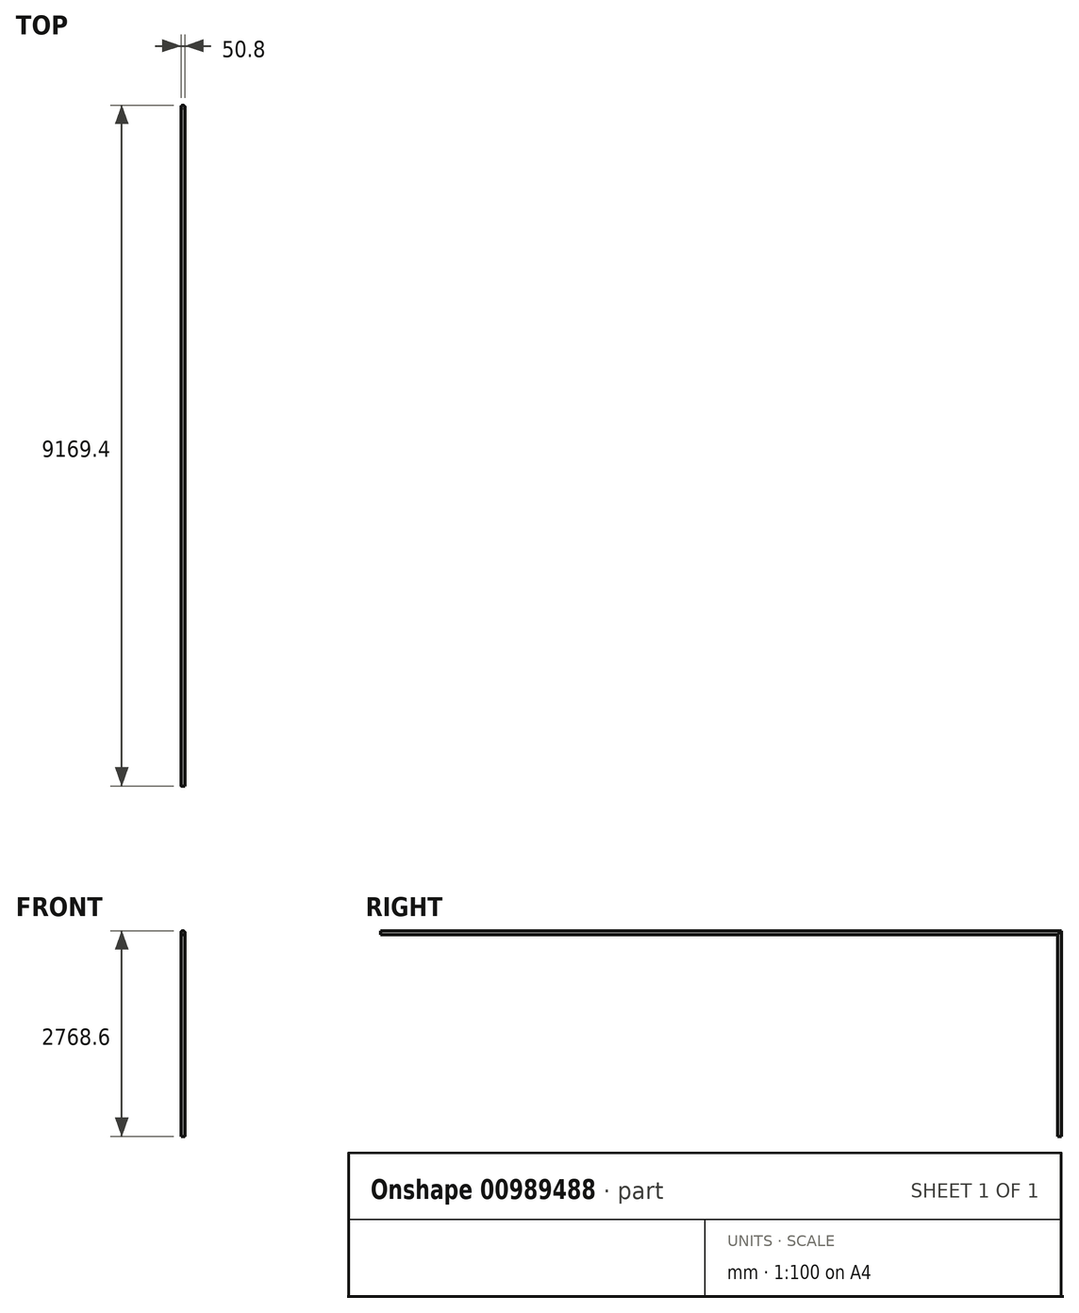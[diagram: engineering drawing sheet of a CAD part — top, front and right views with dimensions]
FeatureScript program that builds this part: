
annotation { "Feature Type Name" : "Feature", "Feature Type Description" : "" }
export const myFeature = defineFeature(function(context is Context, id is Id, definition is map)
    precondition{}
    {
        {
            var Q0;
            Q0=qCreatedBy(makeId("Front.planeOp"),FACE);
            var sketch = newSketch(context, id + "F0", { "sketchPlane" : qUnion([Q0])});
            skCircle(sketch, "E0", {"center": v(0, 0) * mm, "radius": 25.4 * mm});
            skSolve(sketch);
        }
        {
            var Q0;
            Q0=qCreatedBy(makeId("Right.planeOp"),FACE);
            var sketch = newSketch(context, id + "F1", { "sketchPlane" : qUnion([Q0])});
            skLineSegment(sketch, "E1", {"start": v(0, 0) * mm, "end": v(9144, 0) * mm});
            skLineSegment(sketch, "E2", {"start": v(9144, 0) * mm, "end": v(9144, -2743.2) * mm});
            skSolve(sketch);
        }
        {
            var Q0;
            Q0=makeQuery(id+"F0.imprint","IMPRINT",FACE,{"disambiguationData":[TD([[makeQuery(id+"F0.imprint","IMPRINT",EDGE,{"derivedFrom":sQuery(id+"F0.wireOp",EDGE,"E0")}),1.0]])]});
            var Q1;
            Q1=sQuery(id+"F1.wireOp",EDGE,"E1");
            var Q2;
            Q2=sQuery(id+"F1.wireOp",EDGE,"E2");
            sweep(context, id + "F2", {"profiles" : qUnion([Q0]), "path" : qUnion([Q1, Q2])});
        }
    });
